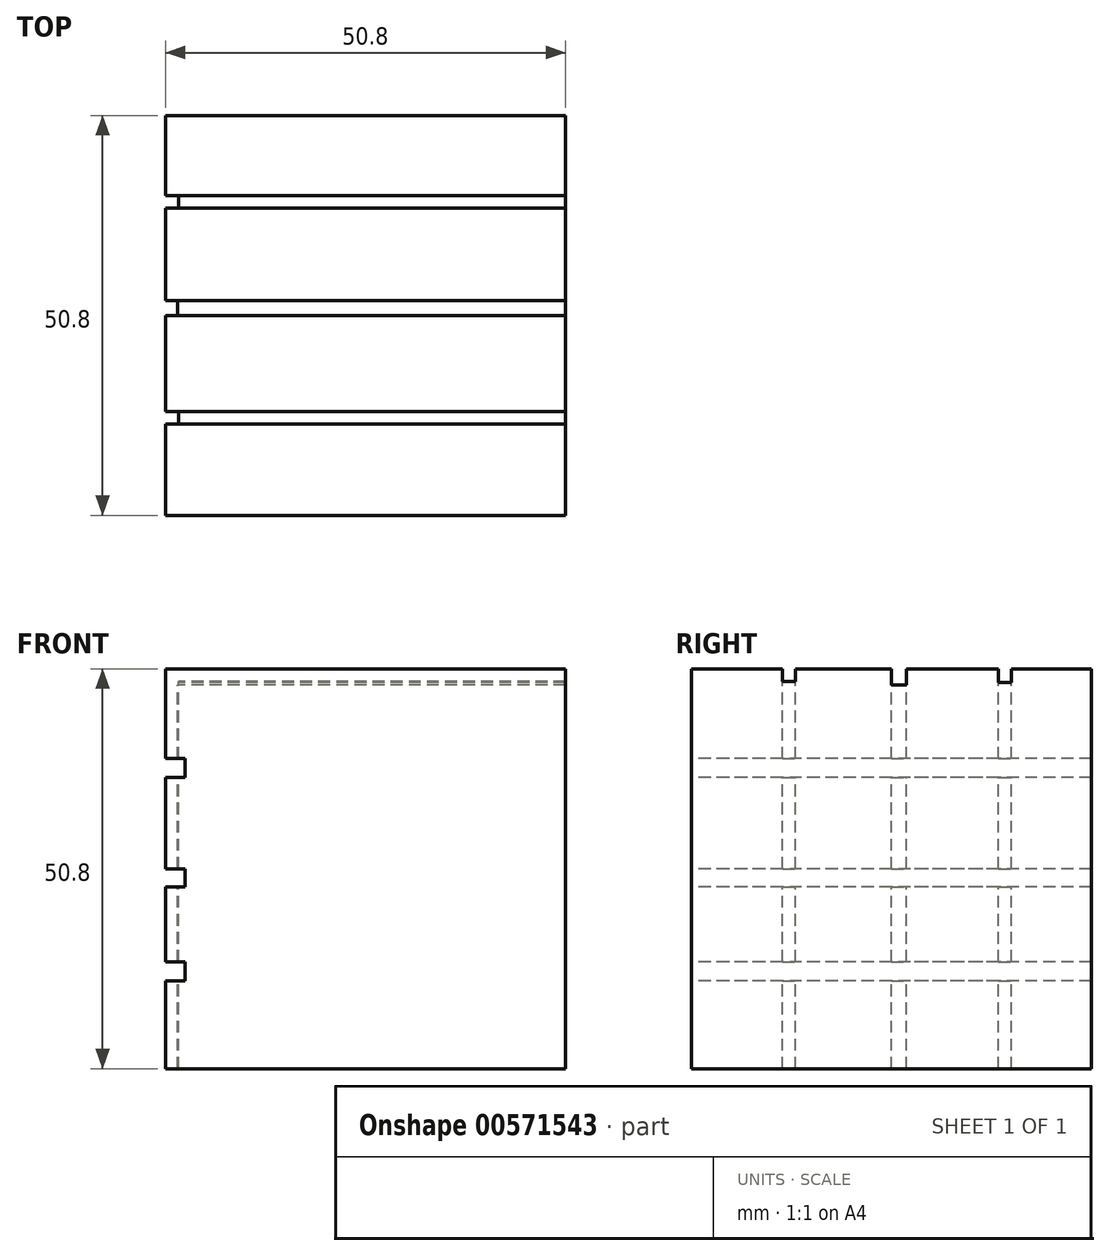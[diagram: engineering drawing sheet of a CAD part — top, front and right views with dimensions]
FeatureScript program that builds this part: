
annotation { "Feature Type Name" : "Feature", "Feature Type Description" : "" }
export const myFeature = defineFeature(function(context is Context, id is Id, definition is map)
    precondition{}
    {
        {
            var Q0;
            Q0=qCreatedBy(makeId("Top.planeOp"),FACE);
            var sketch = newSketch(context, id + "F0", { "sketchPlane" : qUnion([Q0])});
            skLineSegment(sketch, "E0.bottom", {"start": v(-53.71, 56.64) * mm, "end": v(-2.91, 56.64) * mm});
            skLineSegment(sketch, "E0.top", {"start": v(-53.71, 5.84) * mm, "end": v(-2.91, 5.84) * mm});
            skLineSegment(sketch, "E0.left", {"start": v(-53.71, 56.64) * mm, "end": v(-53.71, 5.84) * mm});
            skLineSegment(sketch, "E0.right", {"start": v(-2.91, 56.64) * mm, "end": v(-2.91, 5.84) * mm});
            skSolve(sketch);
        }
        {
            var Q0;
            Q0=makeQuery(id+"F0.imprint","IMPRINT",FACE,{"disambiguationData":[TD([[makeQuery(id+"F0.imprint","IMPRINT",EDGE,{"derivedFrom":sQuery(id+"F0.wireOp",EDGE,"E0.bottom")}),-1.0]])]});
            extrude(context, id + "F1", {"entities" : qUnion([Q0]), "depth" : 50.8 * mm, "offsetDistance" : 25.4 * mm});
        }
        {
            var Q0;
            Q0=makeQuery(id+"F1.opExtrude","SWEPT_FACE",FACE,{"disambiguationData":[OSD([sQuery(id+"F0.wireOp",EDGE,"E0.top")])]});
            var sketch = newSketch(context, id + "F2", { "sketchPlane" : qUnion([Q0])});
            skLineSegment(sketch, "E1.bottom", {"start": v(-53.71, 39.4) * mm, "end": v(-51.24, 39.4) * mm});
            skLineSegment(sketch, "E1.top", {"start": v(-53.71, 37.01) * mm, "end": v(-51.24, 37.01) * mm});
            skLineSegment(sketch, "E1.left", {"start": v(-53.71, 39.4) * mm, "end": v(-53.71, 37.01) * mm});
            skLineSegment(sketch, "E1.right", {"start": v(-51.24, 39.4) * mm, "end": v(-51.24, 37.01) * mm});
            skLineSegment(sketch, "E2.bottom", {"start": v(-53.71, 25.4) * mm, "end": v(-51.24, 25.4) * mm});
            skLineSegment(sketch, "E2.top", {"start": v(-53.71, 23.1) * mm, "end": v(-51.24, 23.1) * mm});
            skLineSegment(sketch, "E2.left", {"start": v(-53.71, 25.4) * mm, "end": v(-53.71, 23.1) * mm});
            skLineSegment(sketch, "E2.right", {"start": v(-51.24, 25.4) * mm, "end": v(-51.24, 23.1) * mm});
            skLineSegment(sketch, "E3.bottom", {"start": v(-53.71, 13.56) * mm, "end": v(-51.24, 13.56) * mm});
            skLineSegment(sketch, "E3.top", {"start": v(-53.71, 11.18) * mm, "end": v(-51.24, 11.18) * mm});
            skLineSegment(sketch, "E3.left", {"start": v(-53.71, 13.56) * mm, "end": v(-53.71, 11.18) * mm});
            skLineSegment(sketch, "E3.right", {"start": v(-51.24, 13.56) * mm, "end": v(-51.24, 11.18) * mm});
            skSolve(sketch);
        }
        {
            var Q0;
            Q0=makeQuery(id+"F2.imprint","IMPRINT",FACE,{"disambiguationData":[TD([[makeQuery(id+"F2.imprint","IMPRINT",EDGE,{"derivedFrom":sQuery(id+"F2.wireOp",EDGE,"E1.bottom")}),-1.0]])]});
            var Q1;
            Q1=makeQuery(id+"F2.imprint","IMPRINT",FACE,{"disambiguationData":[TD([[makeQuery(id+"F2.imprint","IMPRINT",EDGE,{"derivedFrom":sQuery(id+"F2.wireOp",EDGE,"E2.bottom")}),-1.0]])]});
            var Q2;
            Q2=makeQuery(id+"F2.imprint","IMPRINT",FACE,{"disambiguationData":[TD([[makeQuery(id+"F2.imprint","IMPRINT",EDGE,{"derivedFrom":sQuery(id+"F2.wireOp",EDGE,"E3.bottom")}),-1.0]])]});
            extrude(context, id + "F3", {"entities" : qUnion([Q0, Q1, Q2]), "operationType" : NewBodyOperationType.REMOVE, "oppositeDirection" : true, "depth" : 101.6 * mm, "offsetDistance" : 25.4 * mm});
        }
        {
            var Q0;
            Q0=makeQuery(id+"F1.opExtrude","CAP_FACE",FACE,{"disambiguationData":[OSD([sQuery(id+"F0.wireOp",EDGE,"E0.bottom"),sQuery(id+"F0.wireOp",EDGE,"E0.top"),sQuery(id+"F0.wireOp",EDGE,"E0.left"),sQuery(id+"F0.wireOp",EDGE,"E0.right")])],"isStart":false});
            var sketch = newSketch(context, id + "F4", { "sketchPlane" : qUnion([Q0])});
            skPoint(sketch, "E4.oppositeSnap0", {"position": v(-53.71, 31.24) * mm});
            skLineSegment(sketch, "E4.bottom", {"start": v(-53.71, 33.14) * mm, "end": v(-52.17, 33.14) * mm});
            skLineSegment(sketch, "E4.top", {"start": v(-53.71, 31.24) * mm, "end": v(-52.17, 31.24) * mm});
            skLineSegment(sketch, "E4.left", {"start": v(-53.71, 33.14) * mm, "end": v(-53.71, 31.24) * mm});
            skLineSegment(sketch, "E4.right", {"start": v(-52.17, 33.14) * mm, "end": v(-52.17, 31.24) * mm});
            skLineSegment(sketch, "E5.bottom", {"start": v(-53.71, 46.45) * mm, "end": v(-52.05, 46.45) * mm});
            skLineSegment(sketch, "E5.top", {"start": v(-53.71, 44.83) * mm, "end": v(-52.05, 44.83) * mm});
            skLineSegment(sketch, "E5.left", {"start": v(-53.71, 46.45) * mm, "end": v(-53.71, 44.83) * mm});
            skLineSegment(sketch, "E5.right", {"start": v(-52.05, 46.45) * mm, "end": v(-52.05, 44.83) * mm});
            skLineSegment(sketch, "E6.bottom", {"start": v(-53.71, 19.02) * mm, "end": v(-52.05, 19.02) * mm});
            skLineSegment(sketch, "E6.top", {"start": v(-53.71, 17.4) * mm, "end": v(-52.05, 17.4) * mm});
            skLineSegment(sketch, "E6.left", {"start": v(-53.71, 19.02) * mm, "end": v(-53.71, 17.4) * mm});
            skLineSegment(sketch, "E6.right", {"start": v(-52.05, 19.02) * mm, "end": v(-52.05, 17.4) * mm});
            skSolve(sketch);
        }
        {
            var Q0;
            Q0=makeQuery(id+"F4.imprint","IMPRINT",FACE,{"disambiguationData":[TD([[makeQuery(id+"F4.imprint","IMPRINT",EDGE,{"derivedFrom":sQuery(id+"F4.wireOp",EDGE,"E5.bottom")}),-1.0]])]});
            var Q1;
            Q1=makeQuery(id+"F4.imprint","IMPRINT",FACE,{"disambiguationData":[TD([[makeQuery(id+"F4.imprint","IMPRINT",EDGE,{"derivedFrom":sQuery(id+"F4.wireOp",EDGE,"E4.bottom")}),-1.0]])]});
            var Q2;
            Q2=makeQuery(id+"F4.imprint","IMPRINT",FACE,{"disambiguationData":[TD([[makeQuery(id+"F4.imprint","IMPRINT",EDGE,{"derivedFrom":sQuery(id+"F4.wireOp",EDGE,"E6.bottom")}),-1.0]])]});
            extrude(context, id + "F5", {"entities" : qUnion([Q0, Q1, Q2]), "operationType" : NewBodyOperationType.REMOVE, "oppositeDirection" : true, "depth" : 79.5 * mm, "offsetDistance" : 25.4 * mm});
        }
        {
            var Q0;
            Q0=makeQuery(id+"F5.boolean.opBoolean","COPY",FACE,{"disambiguationData":[TD([makeQuery(id+"F3.boolean.opBoolean","COPY",FACE,{"derivedFrom":makeQuery(id+"F3.opExtrude","SWEPT_FACE",FACE,{"disambiguationData":[OSD([sQuery(id+"F2.wireOp",EDGE,"E1.bottom")])]})})])],"derivedFrom":makeQuery(id+"F5.opExtrude","SWEPT_FACE",FACE,{"disambiguationData":[OSD([sQuery(id+"F4.wireOp",EDGE,"E5.right")])]})});
            var sketch = newSketch(context, id + "F6", { "sketchPlane" : qUnion([Q0])});
            skLineSegment(sketch, "E7.bottom", {"start": v(-46.45, 50.8) * mm, "end": v(-44.83, 50.8) * mm});
            skLineSegment(sketch, "E7.top", {"start": v(-46.45, 49.07) * mm, "end": v(-44.83, 49.07) * mm});
            skLineSegment(sketch, "E7.left", {"start": v(-46.45, 50.8) * mm, "end": v(-46.45, 49.07) * mm});
            skLineSegment(sketch, "E7.right", {"start": v(-44.83, 50.8) * mm, "end": v(-44.83, 49.07) * mm});
            skSolve(sketch);
        }
        {
            var Q0;
            Q0=makeQuery(id+"F6.imprint","IMPRINT",FACE,{"disambiguationData":[TD([[makeQuery(id+"F6.imprint","IMPRINT",EDGE,{"derivedFrom":sQuery(id+"F6.wireOp",EDGE,"E7.bottom")}),-1.0]])]});
            extrude(context, id + "F7", {"entities" : qUnion([Q0]), "operationType" : NewBodyOperationType.REMOVE, "oppositeDirection" : true, "depth" : 101.6 * mm, "offsetDistance" : 25.4 * mm});
        }
        {
            var Q0;
            Q0=makeQuery(id+"F5.boolean.opBoolean","COPY",FACE,{"disambiguationData":[TD([makeQuery(id+"F3.boolean.opBoolean","COPY",FACE,{"derivedFrom":makeQuery(id+"F3.opExtrude","SWEPT_FACE",FACE,{"disambiguationData":[OSD([sQuery(id+"F2.wireOp",EDGE,"E1.bottom")])]})})])],"derivedFrom":makeQuery(id+"F5.opExtrude","SWEPT_FACE",FACE,{"disambiguationData":[OSD([sQuery(id+"F4.wireOp",EDGE,"E4.right")])]})});
            var sketch = newSketch(context, id + "F8", { "sketchPlane" : qUnion([Q0])});
            skLineSegment(sketch, "E8.bottom", {"start": v(-33.14, 50.8) * mm, "end": v(-31.24, 50.8) * mm});
            skLineSegment(sketch, "E8.top", {"start": v(-33.14, 48.74) * mm, "end": v(-31.24, 48.74) * mm});
            skLineSegment(sketch, "E8.left", {"start": v(-33.14, 50.8) * mm, "end": v(-33.14, 48.74) * mm});
            skLineSegment(sketch, "E8.right", {"start": v(-31.24, 50.8) * mm, "end": v(-31.24, 48.74) * mm});
            skSolve(sketch);
        }
        {
            var Q0;
            Q0=makeQuery(id+"F8.imprint","IMPRINT",FACE,{"disambiguationData":[TD([[makeQuery(id+"F8.imprint","IMPRINT",EDGE,{"derivedFrom":sQuery(id+"F8.wireOp",EDGE,"E8.bottom")}),-1.0]])]});
            extrude(context, id + "F9", {"entities" : qUnion([Q0]), "operationType" : NewBodyOperationType.REMOVE, "oppositeDirection" : true, "depth" : 101.6 * mm, "offsetDistance" : 25.4 * mm});
        }
        {
            var Q0;
            Q0=makeQuery(id+"F5.boolean.opBoolean","COPY",FACE,{"disambiguationData":[TD([makeQuery(id+"F3.boolean.opBoolean","COPY",FACE,{"derivedFrom":makeQuery(id+"F3.opExtrude","SWEPT_FACE",FACE,{"disambiguationData":[OSD([sQuery(id+"F2.wireOp",EDGE,"E1.bottom")])]})})])],"derivedFrom":makeQuery(id+"F5.opExtrude","SWEPT_FACE",FACE,{"disambiguationData":[OSD([sQuery(id+"F4.wireOp",EDGE,"E6.right")])]})});
            var sketch = newSketch(context, id + "F10", { "sketchPlane" : qUnion([Q0])});
            skLineSegment(sketch, "E9.bottom", {"start": v(-19.02, 50.8) * mm, "end": v(-17.4, 50.8) * mm});
            skLineSegment(sketch, "E9.top", {"start": v(-19.02, 49.19) * mm, "end": v(-17.4, 49.19) * mm});
            skLineSegment(sketch, "E9.left", {"start": v(-19.02, 50.8) * mm, "end": v(-19.02, 49.19) * mm});
            skLineSegment(sketch, "E9.right", {"start": v(-17.4, 50.8) * mm, "end": v(-17.4, 49.19) * mm});
            skSolve(sketch);
        }
        {
            var Q0;
            Q0=makeQuery(id+"F10.imprint","IMPRINT",FACE,{"disambiguationData":[TD([[makeQuery(id+"F10.imprint","IMPRINT",EDGE,{"derivedFrom":sQuery(id+"F10.wireOp",EDGE,"E9.bottom")}),-1.0]])]});
            extrude(context, id + "F11", {"entities" : qUnion([Q0]), "operationType" : NewBodyOperationType.REMOVE, "oppositeDirection" : true, "depth" : 101.6 * mm, "offsetDistance" : 25.4 * mm});
        }
    });
